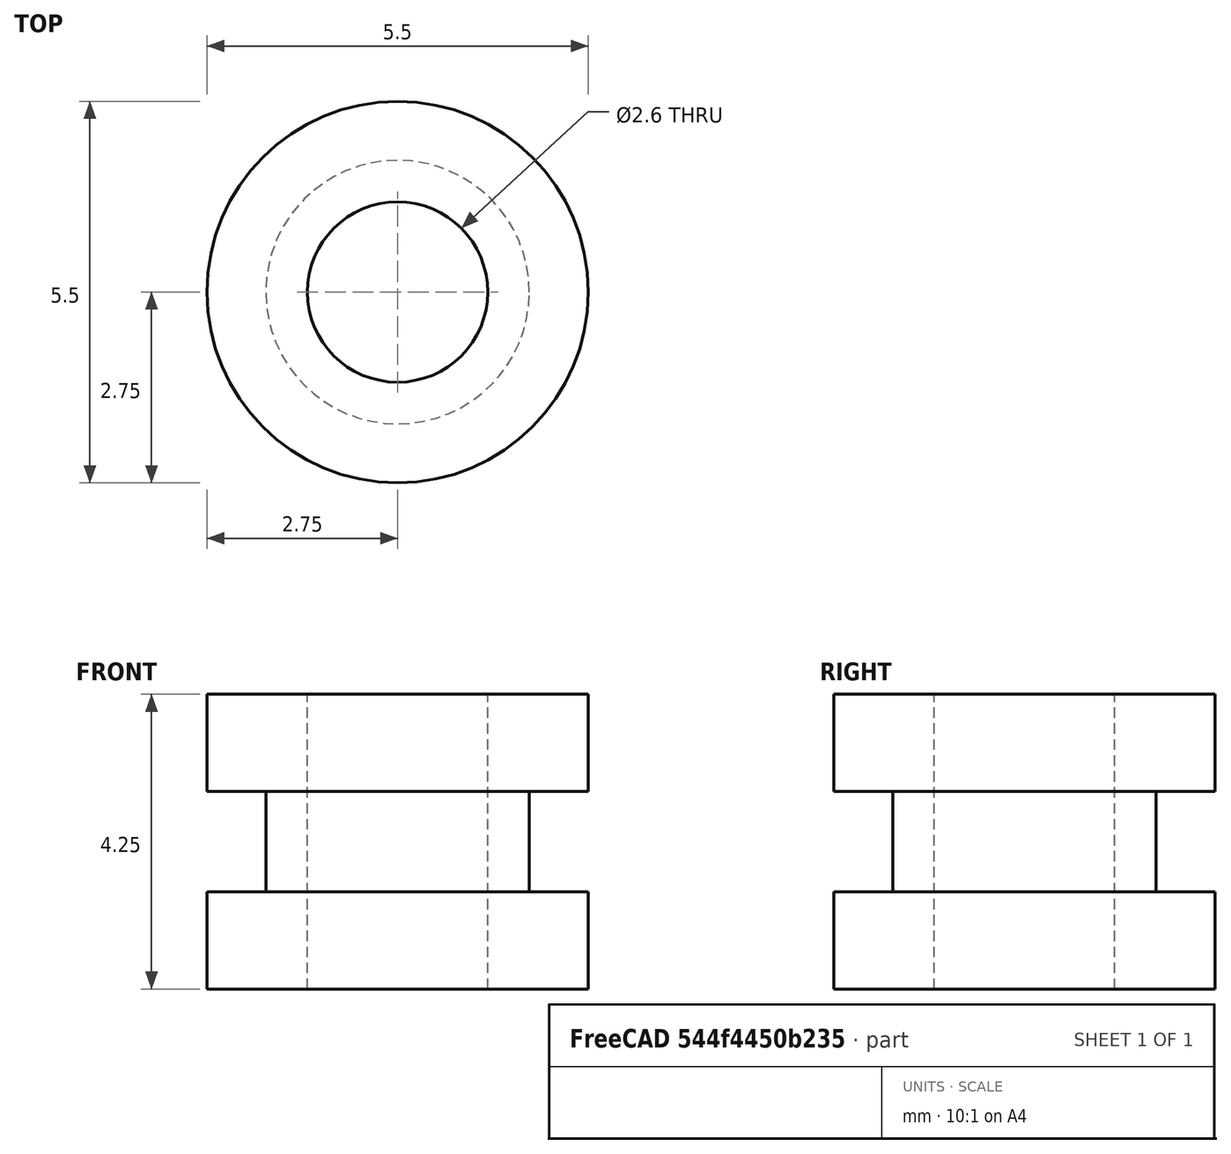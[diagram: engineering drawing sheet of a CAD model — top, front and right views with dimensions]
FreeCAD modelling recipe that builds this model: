
FCSTD DOCUMENT  (FreeCAD 1.0R39285 (Git))
Label: bushing
License: CERN Open Hardware Licence permissive
LicenseURL: https://cern-ohl.web.cern.ch/
objects: Sketcher::SketchObject×1, PartDesign::Revolution×1, PartDesign::Body×1
note: 6 computed .brp shape members not serialized (recipe doc carries the construction recipe); baked Part::Feature solids carry a one-line shape summary decoded from their .brp

FEATURE [Sketcher::SketchObject] Sketch
  ArcFitTolerance = 1e-06
  AttachmentSupport = -> [XZ_Plane]
  FullyConstrained = true
  MakeInternals = false
  MapMode = 5
  Placement = pos=(0,0,0) rot=(1,0,0;1.5708rad)
  sketch-geometry (8):
    g0: LineSegment StartX=-1.3 StartY=0 StartZ=0 EndX=-1.3 EndY=4.25 EndZ=0
    g1: LineSegment StartX=-1.3 StartY=4.25 StartZ=0 EndX=-2.75 EndY=4.25 EndZ=0
    g2: LineSegment StartX=-2.75 StartY=4.25 StartZ=0 EndX=-2.75 EndY=2.85 EndZ=0
    g3: LineSegment StartX=-2.75 StartY=2.85 StartZ=0 EndX=-1.9 EndY=2.85 EndZ=0
    g4: LineSegment StartX=-1.9 StartY=2.85 StartZ=0 EndX=-1.9 EndY=1.4 EndZ=0
    g5: LineSegment StartX=-1.9 StartY=1.4 StartZ=0 EndX=-2.75 EndY=1.4 EndZ=0
    g6: LineSegment StartX=-2.75 StartY=1.4 StartZ=0 EndX=-2.75 EndY=0 EndZ=0
    g7: LineSegment StartX=-2.75 StartY=0 StartZ=0 EndX=-1.3 EndY=0 EndZ=0
  constraints (24):
    c: PointOnObject(g0,g-1)
    c: Vertical(g0)
    c: Coincident(g0,g1)
    c: Horizontal(g1)
    c: Coincident(g1,g2)
    c: Vertical(g2)
    c: Coincident(g2,g3)
    c: Horizontal(g3)
    c: Coincident(g3,g4)
    c: Vertical(g4)
    c: Coincident(g4,g5)
    c: Horizontal(g5)
    c: Coincident(g5,g6)
    c: PointOnObject(g6,g-1)
    c: Coincident(g6,g7)
    c: Coincident(g7,g0)
    c: Distance(g1,g-2) = 2.75
    c: Distance(g0,g-2) = 1.3
    c: Equal(g2,g6)
    c: Equal(g3,g5)
    c: Vertical(g6)
    c: DistanceY(g2,g2) = 1.4
    c: DistanceY(g0,g0) = 4.25
    c: Distance(g3,g-2) = 1.9
FEATURE [PartDesign::Revolution] Revolution
  Angle = 360
  Angle2 = 60
  Axis = (0,2e-16,1)
  Base = (0,0,0)
  Placement = pos=(0,0,0) rot=(1,0,0;1.5708rad)
  Profile = -> Sketch
  ReferenceAxis = -> Sketch [V_Axis]
  Refine = true
  Suppressed = false
  Type = 0
FEATURE [PartDesign::Body] Body
  AllowCompound = false
  Group = -> [Sketch,Revolution]
  Origin = -> Origin
  Tip = -> Revolution
